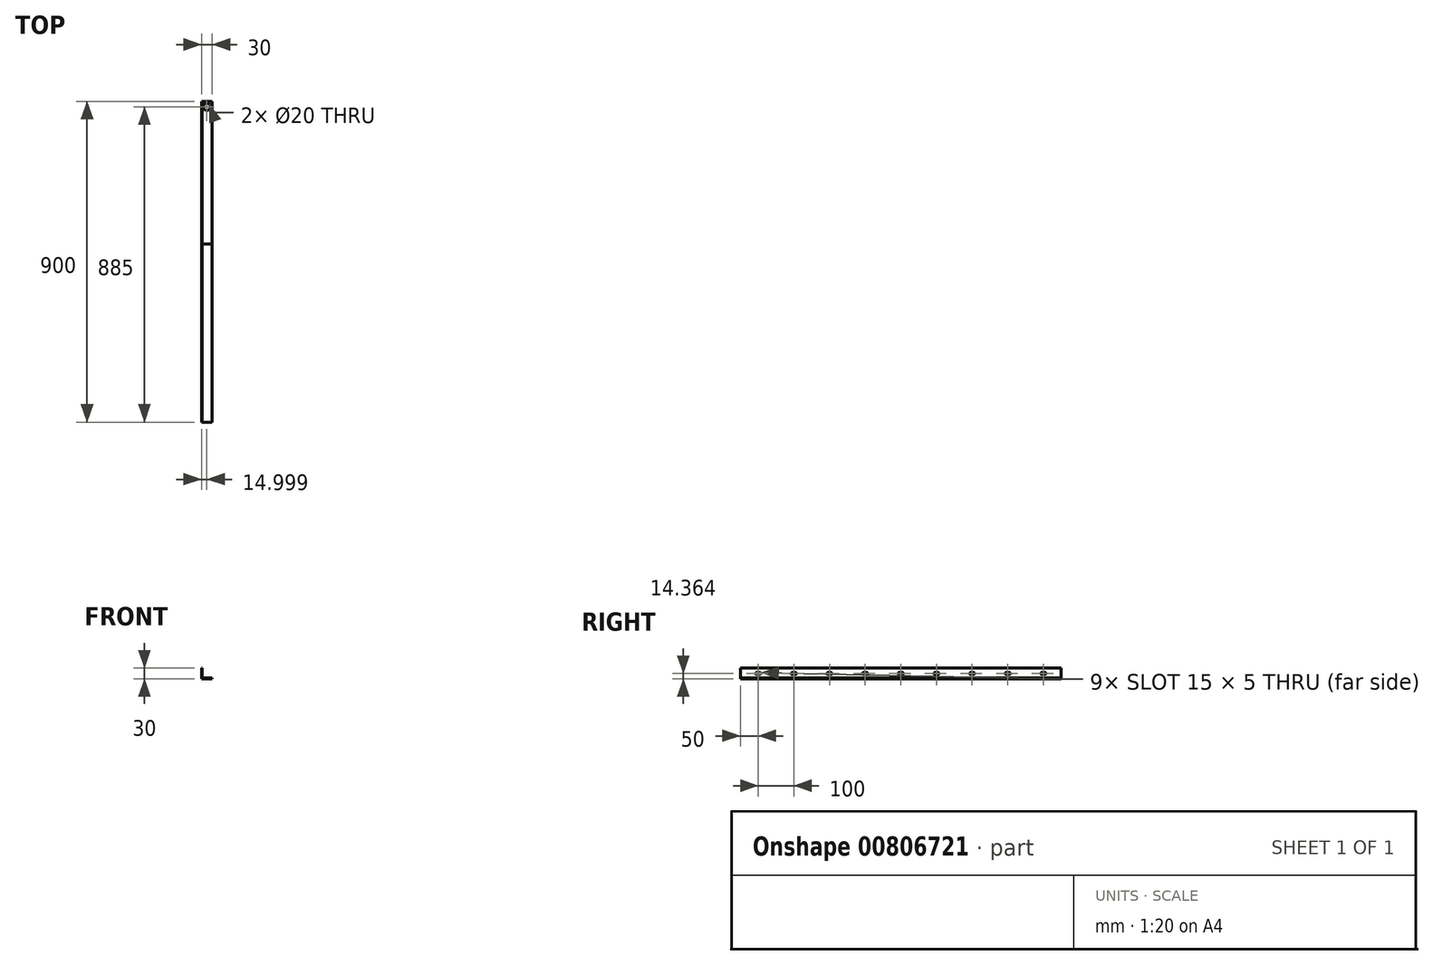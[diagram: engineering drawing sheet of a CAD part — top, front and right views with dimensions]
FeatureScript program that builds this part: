
annotation { "Feature Type Name" : "Feature", "Feature Type Description" : "" }
export const myFeature = defineFeature(function(context is Context, id is Id, definition is map)
    precondition{}
    {
        {
            var Q0;
            Q0=qCreatedBy(makeId("Front.planeOp"),FACE);
            var sketch = newSketch(context, id + "F0", { "sketchPlane" : qUnion([Q0])});
            skLineSegment(sketch, "E0", {"start": v(-8.97, 25.34) * mm, "end": v(-8.97, -4.66) * mm});
            skLineSegment(sketch, "E1", {"start": v(-8.97, -4.66) * mm, "end": v(21.03, -4.66) * mm});
            skLineSegment(sketch, "E2", {"start": v(21.03, -4.66) * mm, "end": v(21.03, -2.66) * mm});
            skLineSegment(sketch, "E3", {"start": v(21.03, -2.66) * mm, "end": v(-6.97, -2.66) * mm});
            skLineSegment(sketch, "E4", {"start": v(-6.97, -2.66) * mm, "end": v(-6.97, 25.34) * mm});
            skLineSegment(sketch, "E5", {"start": v(-6.97, 25.34) * mm, "end": v(-8.97, 25.34) * mm});
            skSolve(sketch);
        }
        {
            var Q0;
            Q0=makeQuery(id+"F0.imprint","IMPRINT",FACE,{"disambiguationData":[TD([[makeQuery(id+"F0.imprint","IMPRINT",EDGE,{"derivedFrom":sQuery(id+"F0.wireOp",EDGE,"E0")}),1.0]])]});
            extrude(context, id + "F1", {"entities" : qUnion([Q0]), "depth" : 400 * mm, "offsetDistance" : 25 * mm});
        }
        {
            var Q0;
            Q0=makeQuery(id+"F1.opExtrude","SWEPT_FACE",FACE,{"disambiguationData":[OSD([sQuery(id+"F0.wireOp",EDGE,"E4")])]});
            var sketch = newSketch(context, id + "F2", { "sketchPlane" : qUnion([Q0])});
            skPoint(sketch, "E6", {"position": v(-350, 9.7) * mm});
            skLineSegment(sketch, "E7", {"start": v(-350, 25.34) * mm, "end": v(-350, -2.66) * mm});
            skLineSegment(sketch, "E8", {"start": v(-350, 9.7) * mm, "end": v(-345, 9.7) * mm});
            skLineSegment(sketch, "E9.MirrorCS", {"start": v(-350, 9.7) * mm, "end": v(-355, 9.7) * mm});
            skArc(sketch, "E10.0.startCap", {"start": v(-350, 12.2) * mm, "mid": v(-347.5, 9.7) * mm, "end": v(-350, 7.2) * mm});
            skArc(sketch, "E10.0.endCap", {"start": v(-355, 7.2) * mm, "mid": v(-357.5, 9.7) * mm, "end": v(-355, 12.2) * mm});
            skLineSegment(sketch, "E10.0.left", {"start": v(-350, 7.2) * mm, "end": v(-355, 7.2) * mm});
            skLineSegment(sketch, "E10.0.right", {"start": v(-350, 12.2) * mm, "end": v(-355, 12.2) * mm});
            skArc(sketch, "E10.1.startCap", {"start": v(-350, 7.2) * mm, "mid": v(-352.5, 9.7) * mm, "end": v(-350, 12.2) * mm});
            skArc(sketch, "E10.1.endCap", {"start": v(-345, 12.2) * mm, "mid": v(-342.5, 9.7) * mm, "end": v(-345, 7.2) * mm});
            skLineSegment(sketch, "E10.1.left", {"start": v(-350, 12.2) * mm, "end": v(-345, 12.2) * mm});
            skLineSegment(sketch, "E10.1.right", {"start": v(-350, 7.2) * mm, "end": v(-345, 7.2) * mm});
            skLineSegment(sketch, "E11.1.0.0", {"start": v(-250, 7.2) * mm, "end": v(-245, 7.2) * mm});
            skArc(sketch, "E11.1.0.1", {"start": v(-245, 12.2) * mm, "mid": v(-242.5, 9.7) * mm, "end": v(-245, 7.2) * mm});
            skLineSegment(sketch, "E11.1.0.2", {"start": v(-250, 12.2) * mm, "end": v(-245, 12.2) * mm});
            skArc(sketch, "E11.1.0.3", {"start": v(-255, 7.2) * mm, "mid": v(-257.5, 9.7) * mm, "end": v(-255, 12.2) * mm});
            skLineSegment(sketch, "E11.1.0.4", {"start": v(-250, 7.2) * mm, "end": v(-255, 7.2) * mm});
            skLineSegment(sketch, "E11.1.0.5", {"start": v(-250, 12.2) * mm, "end": v(-255, 12.2) * mm});
            skLineSegment(sketch, "E11.2.0.0", {"start": v(-150, 7.2) * mm, "end": v(-145, 7.2) * mm});
            skArc(sketch, "E11.2.0.1", {"start": v(-145, 12.2) * mm, "mid": v(-142.5, 9.7) * mm, "end": v(-145, 7.2) * mm});
            skLineSegment(sketch, "E11.2.0.2", {"start": v(-150, 12.2) * mm, "end": v(-145, 12.2) * mm});
            skArc(sketch, "E11.2.0.3", {"start": v(-155, 7.2) * mm, "mid": v(-157.5, 9.7) * mm, "end": v(-155, 12.2) * mm});
            skLineSegment(sketch, "E11.2.0.4", {"start": v(-150, 7.2) * mm, "end": v(-155, 7.2) * mm});
            skLineSegment(sketch, "E11.2.0.5", {"start": v(-150, 12.2) * mm, "end": v(-155, 12.2) * mm});
            skLineSegment(sketch, "E11.3.0.0", {"start": v(-50, 7.2) * mm, "end": v(-45, 7.2) * mm});
            skArc(sketch, "E11.3.0.1", {"start": v(-45, 12.2) * mm, "mid": v(-42.5, 9.7) * mm, "end": v(-45, 7.2) * mm});
            skLineSegment(sketch, "E11.3.0.2", {"start": v(-50, 12.2) * mm, "end": v(-45, 12.2) * mm});
            skArc(sketch, "E11.3.0.3", {"start": v(-55, 7.2) * mm, "mid": v(-57.5, 9.7) * mm, "end": v(-55, 12.2) * mm});
            skLineSegment(sketch, "E11.3.0.4", {"start": v(-50, 7.2) * mm, "end": v(-55, 7.2) * mm});
            skLineSegment(sketch, "E11.3.0.5", {"start": v(-50, 12.2) * mm, "end": v(-55, 12.2) * mm});
            skArc(sketch, "E12.1.0.0", {"start": v(-445, 12.2) * mm, "mid": v(-442.5, 9.7) * mm, "end": v(-445, 7.2) * mm});
            skLineSegment(sketch, "E12.1.0.1", {"start": v(-450, 7.2) * mm, "end": v(-445, 7.2) * mm});
            skLineSegment(sketch, "E12.1.0.2", {"start": v(-450, 12.2) * mm, "end": v(-445, 12.2) * mm});
            skArc(sketch, "E12.1.0.3", {"start": v(-455, 7.2) * mm, "mid": v(-457.5, 9.7) * mm, "end": v(-455, 12.2) * mm});
            skLineSegment(sketch, "E12.1.0.4", {"start": v(-450, 12.2) * mm, "end": v(-455, 12.2) * mm});
            skLineSegment(sketch, "E12.1.0.5", {"start": v(-450, 7.2) * mm, "end": v(-455, 7.2) * mm});
            skArc(sketch, "E12.2.0.0", {"start": v(-545, 12.2) * mm, "mid": v(-542.5, 9.7) * mm, "end": v(-545, 7.2) * mm});
            skLineSegment(sketch, "E12.2.0.1", {"start": v(-550, 7.2) * mm, "end": v(-545, 7.2) * mm});
            skLineSegment(sketch, "E12.2.0.2", {"start": v(-550, 12.2) * mm, "end": v(-545, 12.2) * mm});
            skArc(sketch, "E12.2.0.3", {"start": v(-555, 7.2) * mm, "mid": v(-557.5, 9.7) * mm, "end": v(-555, 12.2) * mm});
            skLineSegment(sketch, "E12.2.0.4", {"start": v(-550, 12.2) * mm, "end": v(-555, 12.2) * mm});
            skLineSegment(sketch, "E12.2.0.5", {"start": v(-550, 7.2) * mm, "end": v(-555, 7.2) * mm});
            skArc(sketch, "E12.3.0.0", {"start": v(-645, 12.2) * mm, "mid": v(-642.5, 9.7) * mm, "end": v(-645, 7.2) * mm});
            skLineSegment(sketch, "E12.3.0.1", {"start": v(-650, 7.2) * mm, "end": v(-645, 7.2) * mm});
            skLineSegment(sketch, "E12.3.0.2", {"start": v(-650, 12.2) * mm, "end": v(-645, 12.2) * mm});
            skArc(sketch, "E12.3.0.3", {"start": v(-655, 7.2) * mm, "mid": v(-657.5, 9.7) * mm, "end": v(-655, 12.2) * mm});
            skLineSegment(sketch, "E12.3.0.4", {"start": v(-650, 12.2) * mm, "end": v(-655, 12.2) * mm});
            skLineSegment(sketch, "E12.3.0.5", {"start": v(-650, 7.2) * mm, "end": v(-655, 7.2) * mm});
            skArc(sketch, "E12.4.0.0", {"start": v(-745, 12.2) * mm, "mid": v(-742.5, 9.7) * mm, "end": v(-745, 7.2) * mm});
            skLineSegment(sketch, "E12.4.0.1", {"start": v(-750, 7.2) * mm, "end": v(-745, 7.2) * mm});
            skLineSegment(sketch, "E12.4.0.2", {"start": v(-750, 12.2) * mm, "end": v(-745, 12.2) * mm});
            skArc(sketch, "E12.4.0.3", {"start": v(-755, 7.2) * mm, "mid": v(-757.5, 9.7) * mm, "end": v(-755, 12.2) * mm});
            skLineSegment(sketch, "E12.4.0.4", {"start": v(-750, 12.2) * mm, "end": v(-755, 12.2) * mm});
            skLineSegment(sketch, "E12.4.0.5", {"start": v(-750, 7.2) * mm, "end": v(-755, 7.2) * mm});
            skArc(sketch, "E12.5.0.0", {"start": v(-845, 12.2) * mm, "mid": v(-842.5, 9.7) * mm, "end": v(-845, 7.2) * mm});
            skLineSegment(sketch, "E12.5.0.1", {"start": v(-850, 7.2) * mm, "end": v(-845, 7.2) * mm});
            skLineSegment(sketch, "E12.5.0.2", {"start": v(-850, 12.2) * mm, "end": v(-845, 12.2) * mm});
            skArc(sketch, "E12.5.0.3", {"start": v(-855, 7.2) * mm, "mid": v(-857.5, 9.7) * mm, "end": v(-855, 12.2) * mm});
            skLineSegment(sketch, "E12.5.0.4", {"start": v(-850, 12.2) * mm, "end": v(-855, 12.2) * mm});
            skLineSegment(sketch, "E12.5.0.5", {"start": v(-850, 7.2) * mm, "end": v(-855, 7.2) * mm});
            skLineSegment(sketch, "E12.direction1", {"start": v(-355, 7.2) * mm, "end": v(-455, 7.2) * mm, "construction": true});
            skSolve(sketch);
        }
        {
            var Q0;
            Q0=makeQuery(id+"F2.imprint","IMPRINT",FACE,{"disambiguationData":[TD([[makeQuery(id+"F2.imprint","IMPRINT",EDGE,{"derivedFrom":sQuery(id+"F2.wireOp",EDGE,"E10.0.endCap")}),-1.0]])]});
            var Q1;
            {var subQ0=sQuery(id+"F2.wireOp",EDGE,"E8");var subQ3=sQuery(id+"F2.wireOp",EDGE,"E10.0.startCap");var subQ5=makeQuery(id+"F2.imprint","INTERSECT",VERTEX,{"derivedFrom":[subQ0,subQ3]});Q1=makeQuery(id+"F2.imprint","IMPRINT",FACE,{"disambiguationData":[TD([[makeQuery(id+"F2.imprint","IMPRINT",EDGE,{"disambiguationData":[TD([[subQ5,1.0]])],"derivedFrom":subQ0}),-1.0]])]});}
            var Q2;
            {var subQ0=sQuery(id+"F2.wireOp",EDGE,"E9.MirrorCS");var subQ3=sQuery(id+"F2.wireOp",EDGE,"E10.1.startCap");var subQ5=makeQuery(id+"F2.imprint","INTERSECT",VERTEX,{"derivedFrom":[subQ0,subQ3]});Q2=makeQuery(id+"F2.imprint","IMPRINT",FACE,{"disambiguationData":[TD([[makeQuery(id+"F2.imprint","IMPRINT",EDGE,{"disambiguationData":[TD([[subQ5,1.0]])],"derivedFrom":subQ0}),1.0]])]});}
            var Q3;
            {var subQ0=sQuery(id+"F2.wireOp",EDGE,"E8");var subQ3=sQuery(id+"F2.wireOp",EDGE,"E10.0.startCap");var subQ5=makeQuery(id+"F2.imprint","INTERSECT",VERTEX,{"derivedFrom":[subQ0,subQ3]});Q3=makeQuery(id+"F2.imprint","IMPRINT",FACE,{"disambiguationData":[TD([[makeQuery(id+"F2.imprint","IMPRINT",EDGE,{"disambiguationData":[TD([[subQ5,1.0]])],"derivedFrom":subQ0}),1.0]])]});}
            var Q4;
            Q4=makeQuery(id+"F2.imprint","IMPRINT",FACE,{"disambiguationData":[TD([[makeQuery(id+"F2.imprint","IMPRINT",EDGE,{"derivedFrom":sQuery(id+"F2.wireOp",EDGE,"E10.1.endCap")}),-1.0]])]});
            var Q5;
            {var subQ0=sQuery(id+"F2.wireOp",EDGE,"E9.MirrorCS");var subQ3=sQuery(id+"F2.wireOp",EDGE,"E10.1.startCap");var subQ5=makeQuery(id+"F2.imprint","INTERSECT",VERTEX,{"derivedFrom":[subQ0,subQ3]});Q5=makeQuery(id+"F2.imprint","IMPRINT",FACE,{"disambiguationData":[TD([[makeQuery(id+"F2.imprint","IMPRINT",EDGE,{"disambiguationData":[TD([[subQ5,1.0]])],"derivedFrom":subQ0}),-1.0]])]});}
            var Q6;
            Q6=makeQuery(id+"F2.imprint","IMPRINT",FACE,{"disambiguationData":[TD([[makeQuery(id+"F2.imprint","IMPRINT",EDGE,{"derivedFrom":sQuery(id+"F2.wireOp",EDGE,"E11.1.0.0")}),1.0]])]});
            var Q7;
            Q7=makeQuery(id+"F2.imprint","IMPRINT",FACE,{"disambiguationData":[TD([[makeQuery(id+"F2.imprint","IMPRINT",EDGE,{"derivedFrom":sQuery(id+"F2.wireOp",EDGE,"E11.2.0.0")}),1.0]])]});
            var Q8;
            Q8=makeQuery(id+"F2.imprint","IMPRINT",FACE,{"disambiguationData":[TD([[makeQuery(id+"F2.imprint","IMPRINT",EDGE,{"derivedFrom":sQuery(id+"F2.wireOp",EDGE,"E11.3.0.0")}),1.0]])]});
            extrude(context, id + "F3", {"entities" : qUnion([Q0, Q1, Q2, Q3, Q4, Q5, Q6, Q7, Q8]), "operationType" : NewBodyOperationType.REMOVE, "oppositeDirection" : true, "depth" : 2 * mm, "offsetDistance" : 25 * mm});
        }
        {
            var Q0;
            Q0 = qSketchRegion(id + "F0", true);
            extrude(context, id + "F4", {"entities" : qUnion([Q0]), "depth" : 900 * mm, "offsetDistance" : 25 * mm});
        }
        {
            var Q0;
            Q0 = qSketchRegion(id + "F2", true);
            extrude(context, id + "F5", {"entities" : qUnion([Q0]), "operationType" : NewBodyOperationType.REMOVE, "oppositeDirection" : true, "depth" : 2 * mm, "offsetDistance" : 25 * mm});
        }
        {
            var Q0;
            Q0=makeQuery(id+"F4.opExtrude","SWEPT_FACE",FACE,{"disambiguationData":[OSD([sQuery(id+"F0.wireOp",EDGE,"E1")])]});
            var sketch = newSketch(context, id + "F6", { "sketchPlane" : qUnion([Q0])});
            skCircle(sketch, "E13", {"center": v(6.03, 15) * mm, "radius": 10 * mm});
            skPoint(sketch, "E13.centerSnap0", {"position": v(6.03, 0) * mm});
            skSolve(sketch);
        }
        {
            var Q0;
            Q0=makeQuery(id+"F6.imprint","IMPRINT",FACE,{"disambiguationData":[TD([[makeQuery(id+"F6.imprint","IMPRINT",EDGE,{"derivedFrom":sQuery(id+"F6.wireOp",EDGE,"E13")}),1.0]])]});
            var Q1;
            Q1=sQuery(id+"F6.wireOp",EDGE,"E13");
            extrude(context, id + "F7", {"entities" : qUnion([Q0]), "operationType" : NewBodyOperationType.REMOVE, "surfaceEntities" : qUnion([Q1]), "oppositeDirection" : true, "depth" : 2 * mm, "offsetDistance" : 25 * mm});
        }
    });
